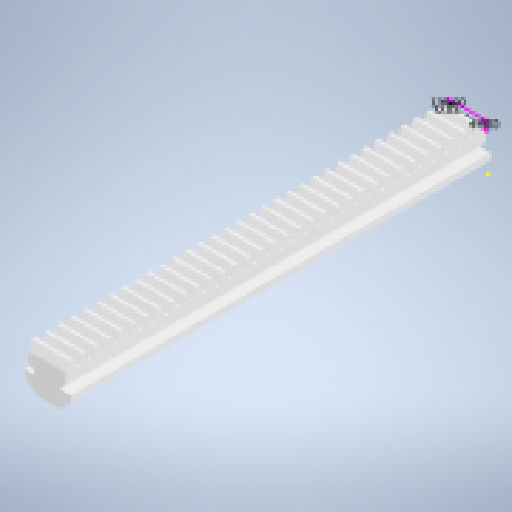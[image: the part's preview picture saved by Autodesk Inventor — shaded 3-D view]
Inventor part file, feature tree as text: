
AUTODESK INVENTOR PART (.ipt)
format: ipt  version: 2023.2 (Build 272271000, 271)  size: 985,600 bytes
history: native  units: mm
features: sketch x3, extrude x2, projected_geometry x1
ambient origin geometry x8: Origin, YZ Plane, XZ Plane, XY Plane, X Axis, Y Axis, Z Axis, Center Point
bodies: Body1 (feature_tree)
feature tree (6):
  extrude  "Extrusion3"  Depth=0.15mm
  sketch  "Sketch5"  dims[d11=0.15mm d12=98.27mm d13=0.0mm]
  extrude  "Extrusion7"  Depth=98.27mm TaperAngle=0.0deg
  sketch  "Sketch1"  dims[d9=0.15mm d10=0.15mm]
  sketch  "Sketch7"  dims[d32=0.85mm d36=7.679449mm d37=23.736478mm d68=4.4mm d69=2.3mm d70=0.672mm d71=12.217305mm d72=12.217305mm d73=2.978358mm d74=330.0mm d76=2.978mm d77=10.0mm d79=10.0mm d81=98.27mm d82=0.0mm d61=1.0mm d62=1.0mm d63=1.0mm d64=0.15mm d65=0.25mm d66=0.375mm d67=14.3117mm]
  projected_geometry  "Projected Loop2"
